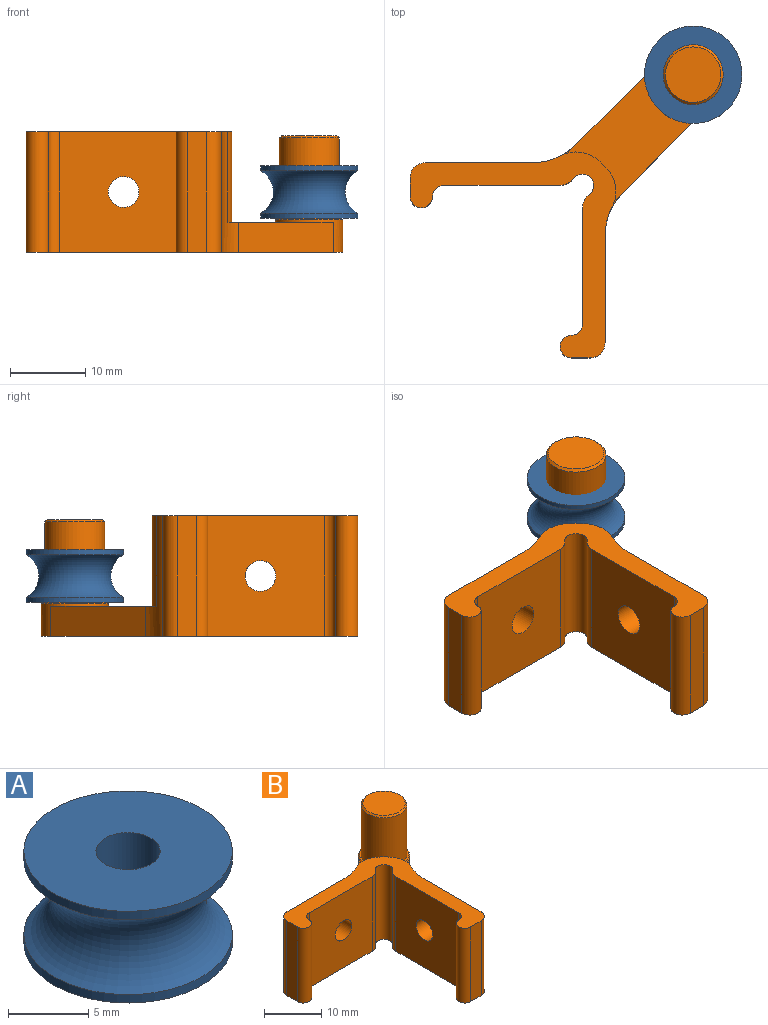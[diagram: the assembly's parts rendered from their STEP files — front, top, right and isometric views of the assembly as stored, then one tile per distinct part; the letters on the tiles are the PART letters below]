
ASSEMBLY  parts=2 mates=1
PART A: 6 faces, bbox 17.4x17.4x7 mm
  f0: torus R=8.05mm, axis (0,0,1), area 236.3mm2, adj f1,f5
  f1: cylinder r=6.5mm len=13mm, axis (0,0,1), area 26.3mm2, adj f0,f2
  f2: plane 13x13mm, normal (0,0,-1), area 120.2mm2, adj f1,f3
  f3: cylinder r=2mm len=7mm, axis (0,0,1), area 88mm2, adj f2,f4
  f4: plane 13x13mm, normal (0,0,1), area 120.2mm2, adj f3,f5
  f5: cylinder r=6.5mm len=13mm, axis (0,0,1), area 26.3mm2, adj f0,f4
PART B: 35 faces, bbox 42.2x42.2x16 mm
  f0: cylinder r=1.5mm len=16mm, axis (0,0,-1), area 37.7mm2, adj f1,f21,f23,f32
  f1: plane 16x15.55mm, normal (0,-1,0), area 235.6mm2, adj f0,f2,f23,f32,f33
  f2: cylinder r=2mm len=16mm, axis (0,0,-1), area 25.1mm2, adj f1,f3,f23,f32
  f3: plane 16x0.48mm, normal (0.71,-0.71,0), area 10.7mm2, adj f2,f4,f23,f32
  f4: cylinder r=1.5mm len=16mm, axis (0,0,-1), area 75.4mm2, adj f3,f5,f23,f32
  f5: plane 16x0.48mm, normal (-0.71,0.71,0), area 10.7mm2, adj f4,f6,f23,f32
  f6: cylinder r=2mm len=16mm, axis (0,0,-1), area 25.1mm2, adj f5,f7,f23,f32
  f7: plane 16x15.55mm, normal (-1,0,0), area 235.6mm2, adj f6,f8,f23,f32,f34
  f8: cylinder r=1.5mm len=16mm, axis (0,0,-1), area 37.7mm2, adj f7,f9,f23,f32
  f9: cylinder r=1.5mm len=16mm, axis (0,0,-1), area 75.4mm2, adj f8,f10,f23,f32
  f10: plane 16x2.5mm, normal (0,-1,0), area 40mm2, adj f9,f11,f23,f32
  f11: cylinder r=2mm len=16mm, axis (0,0,-1), area 50.3mm2, adj f10,f12,f23,f32
  f12: plane 16x14.32mm, normal (1,0,0), area 216mm2, adj f11,f13,f23,f32,f34
  f13: cylinder r=8mm len=16mm, axis (0,0,-1), area 71.7mm2, adj f12,f14,f22,f23,f29,f32
  f14: plane 12.59x12.59mm, normal (0.71,-0.71,0), area 71.2mm2, adj f13,f15,f22,f23
  f15: cylinder r=4.5mm len=9mm, axis (0,0,-1), area 65mm2, adj f14,f16,f22,f23,f25
  f16: plane 12.59x12.59mm, normal (-0.71,0.71,0), area 71.2mm2, adj f15,f17,f22,f23
  f17: cylinder r=8mm len=16mm, axis (0,0,-1), area 71.7mm2, adj f16,f18,f22,f23,f31,f32
  f18: plane 16x14.32mm, normal (0,1,0), area 216mm2, adj f17,f19,f23,f32,f33
  f19: cylinder r=2mm len=16mm, axis (0,0,-1), area 50.3mm2, adj f18,f20,f23,f32
  f20: plane 16x2.5mm, normal (-1,0,0), area 40mm2, adj f19,f21,f23,f32
  f21: cylinder r=1.5mm len=16mm, axis (0,0,-1), area 75.4mm2, adj f0,f20,f23,f32
  f22: plane 20.88x20.88mm, normal (0,0,1), area 126.7mm2, adj f13,f14,f15,f16,f17,f29,f30,f31
  f23: plane 42.25x42.25mm, normal (0,0,-1), area 360.7mm2, adj f0,f1,f2,f3,f4,f5,f6,f7
  f24: plane 8.6x8.6mm, normal (0,0,1), area 7.8mm2, adj f25,f26
  f25: cone r=4.3mm half-angle=45deg, axis (0,0,-1), area 7.8mm2, adj f15,f24
  f26: cylinder r=4mm len=10.7mm, axis (0,0,-1), area 268.9mm2, adj f24,f28
  f27: plane 7.4x7.4mm, normal (0,0,1), area 43mm2, adj f28
  f28: cone r=3.7mm half-angle=45deg, axis (0,0,-1), area 10.3mm2, adj f26,f27
  f29: cylinder r=4.5mm len=12mm, axis (0,0,-1), area 68.7mm2, adj f13,f22,f30,f32
  f30: plane 12x0.79mm, normal (0.71,0.71,0), area 13.4mm2, adj f22,f29,f31,f32
  f31: cylinder r=4.5mm len=12mm, axis (0,0,-1), area 68.7mm2, adj f17,f22,f30,f32
  f32: plane 27.44x27.44mm, normal (0,0,1), area 170.4mm2, adj f0,f1,f2,f3,f4,f5,f6,f7
  f33: cylinder r=2.05mm len=4.1mm, axis (0,1,0), area 38.6mm2, adj f1,f18
  f34: cylinder r=2.05mm len=4.1mm, axis (1,0,0), area 38.6mm2, adj f7,f12
PLACE A t=(3.67,39.38,12.88)mm
PLACE B t=(-21.08,14.63,4.88)mm
MATE fastened A.f0 <-> B.f15  axis (0,0,-1) through (3.67,39.38,9.38)mm
